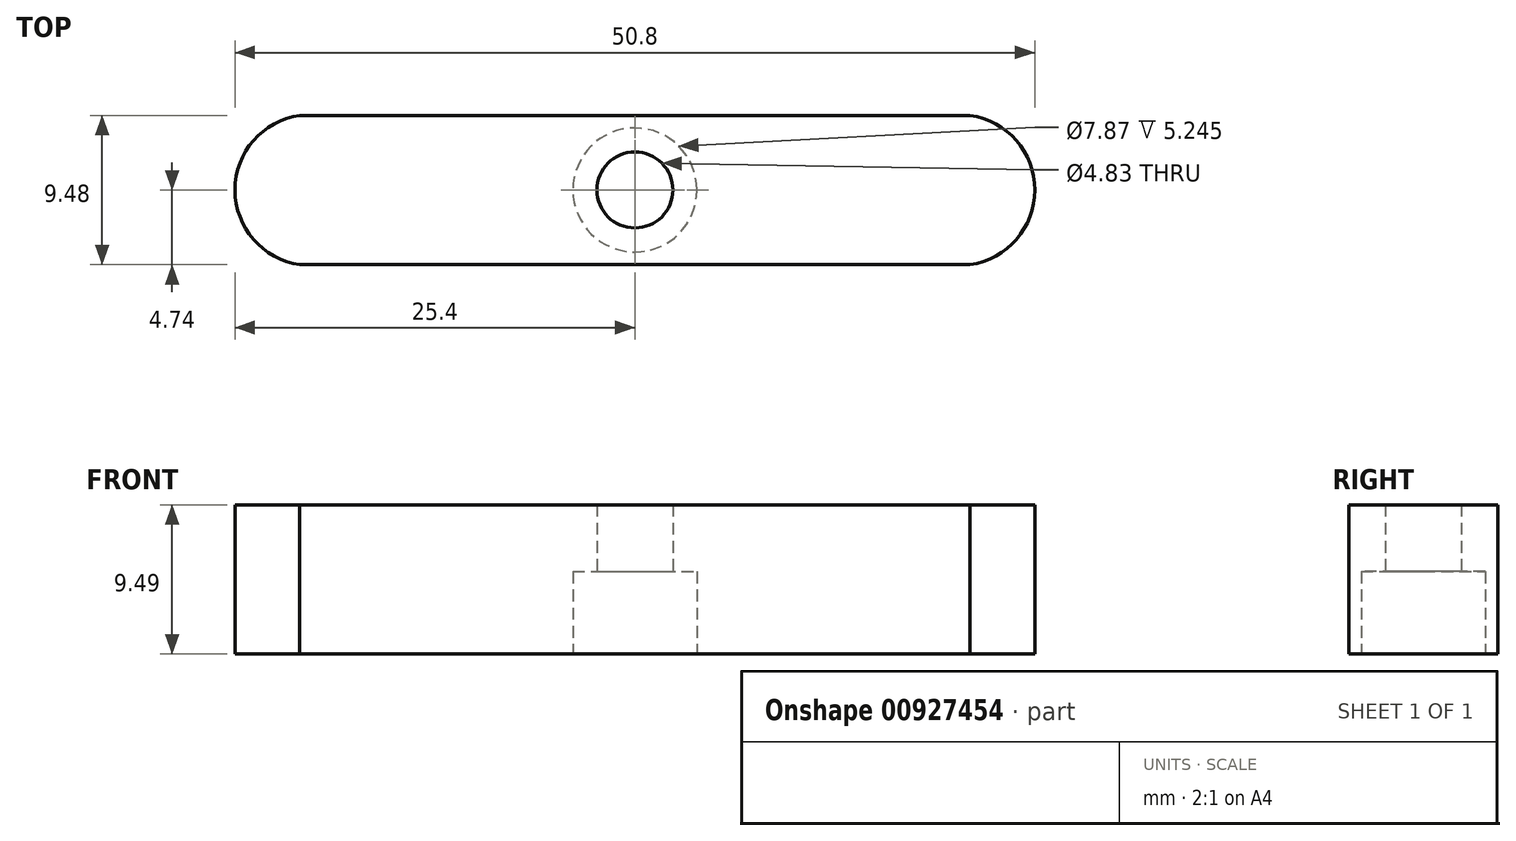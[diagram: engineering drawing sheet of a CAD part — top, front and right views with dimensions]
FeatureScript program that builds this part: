
annotation { "Feature Type Name" : "Feature", "Feature Type Description" : "" }
export const myFeature = defineFeature(function(context is Context, id is Id, definition is map)
    precondition{}
    {
        {
            var Q0;
            Q0=qCreatedBy(makeId("Top.planeOp"),FACE);
            var sketch = newSketch(context, id + "F0", { "sketchPlane" : qUnion([Q0])});
            skLineSegment(sketch, "E0.bottom", {"start": v(-21.28, 4.74) * mm, "end": v(21.28, 4.74) * mm});
            skLineSegment(sketch, "E0.top", {"start": v(-21.28, -4.74) * mm, "end": v(21.28, -4.74) * mm});
            skPoint(sketch, "E0.middle", {"position": v(0, 0) * mm});
            skArc(sketch, "E1", {"start": v(-21.28, 4.74) * mm, "mid": v(-25.4, 0) * mm, "end": v(-21.28, -4.74) * mm});
            skArc(sketch, "E2", {"start": v(21.28, -4.74) * mm, "mid": v(25.4, 0) * mm, "end": v(21.28, 4.74) * mm});
            skSolve(sketch);
        }
        {
            var Q0;
            Q0 = qSketchRegion(id + "F0", true);
            extrude(context, id + "F1", {"entities" : qUnion([Q0]), "depth" : 9.5 * mm, "offsetDistance" : 25.4 * mm});
        }
        {
            var Q0;
            Q0=makeQuery(id+"F1.opExtrude","CAP_FACE",FACE,{"disambiguationData":[OSD([sQuery(id+"F0.wireOp",EDGE,"E0.bottom"),sQuery(id+"F0.wireOp",EDGE,"E0.top"),sQuery(id+"F0.wireOp",EDGE,"E1"),sQuery(id+"F0.wireOp",EDGE,"E2")])],"isStart":true});
            var sketch = newSketch(context, id + "F2", { "sketchPlane" : qUnion([Q0])});
            skCircle(sketch, "E3", {"center": v(0, 0) * mm, "radius": 3.94 * mm});
            skSolve(sketch);
        }
        {
            var Q0;
            Q0 = qSketchRegion(id + "F2", true);
            extrude(context, id + "F3", {"entities" : qUnion([Q0]), "operationType" : NewBodyOperationType.REMOVE, "oppositeDirection" : true, "depth" : 5.25 * mm, "offsetDistance" : 25.4 * mm});
        }
        {
            var Q0;
            Q0=makeQuery(id+"F3.boolean.opBoolean","COPY",FACE,{"derivedFrom":makeQuery(id+"F3.opExtrude","CAP_FACE",FACE,{"disambiguationData":[OSD([sQuery(id+"F2.wireOp",EDGE,"E3")])],"isStart":false})});
            var sketch = newSketch(context, id + "F4", { "sketchPlane" : qUnion([Q0])});
            skCircle(sketch, "E4", {"center": v(0, 0) * mm, "radius": 2.41 * mm});
            skSolve(sketch);
        }
        {
            var Q0;
            Q0 = qSketchRegion(id + "F4", true);
            extrude(context, id + "F5", {"entities" : qUnion([Q0]), "operationType" : NewBodyOperationType.REMOVE, "endBound" : BoundingType.THROUGH_ALL, "oppositeDirection" : true, "depth" : 25.4 * mm, "offsetDistance" : 25.4 * mm});
        }
    });
